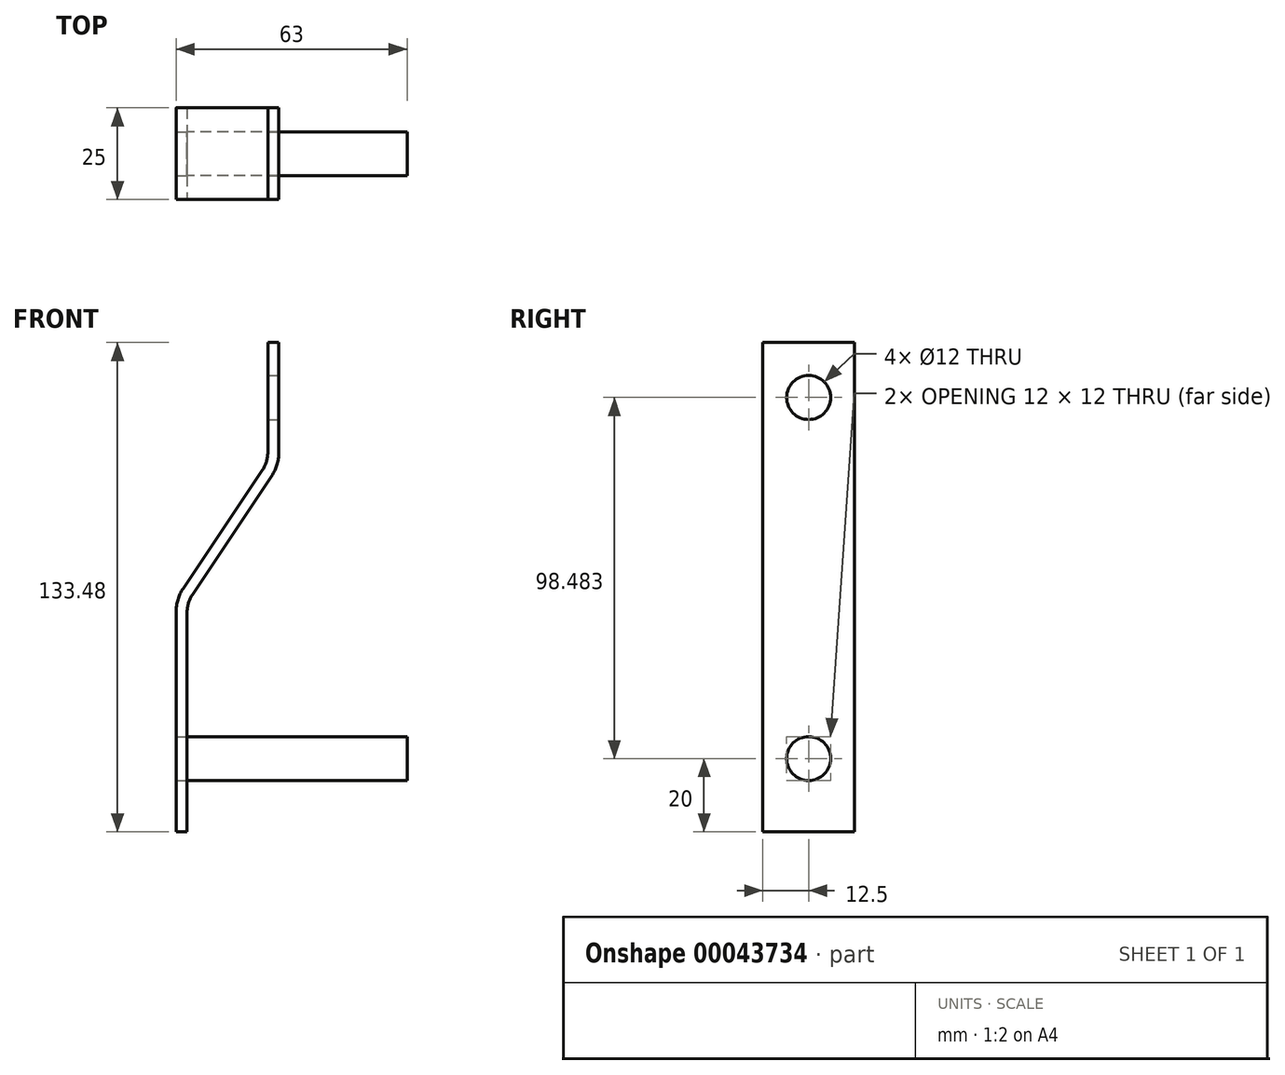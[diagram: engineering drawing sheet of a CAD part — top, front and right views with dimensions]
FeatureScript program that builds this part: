
annotation { "Feature Type Name" : "Feature", "Feature Type Description" : "" }
export const myFeature = defineFeature(function(context is Context, id is Id, definition is map)
    precondition{}
    {
        {
            var Q0;
            Q0=qCreatedBy(makeId("Top.planeOp"),FACE);
            var sketch = newSketch(context, id + "F0", { "sketchPlane" : qUnion([Q0])});
            skLineSegment(sketch, "E0.bottom", {"start": v(-1.5, 12.5) * mm, "end": v(1.5, 12.5) * mm});
            skLineSegment(sketch, "E0.top", {"start": v(-1.5, -12.5) * mm, "end": v(1.5, -12.5) * mm});
            skLineSegment(sketch, "E0.left", {"start": v(-1.5, 12.5) * mm, "end": v(-1.5, -12.5) * mm});
            skLineSegment(sketch, "E0.right", {"start": v(1.5, 12.5) * mm, "end": v(1.5, -12.5) * mm});
            skSolve(sketch);
        }
        {
            var Q0;
            Q0=qCreatedBy(makeId("Front.planeOp"),FACE);
            var sketch = newSketch(context, id + "F1", { "sketchPlane" : qUnion([Q0])});
            skLineSegment(sketch, "E1", {"start": v(0, 0) * mm, "end": v(0, 60) * mm});
            skLineSegment(sketch, "E2", {"start": v(1.69, 65.56) * mm, "end": v(23.31, 97.93) * mm});
            skLineSegment(sketch, "E3", {"start": v(25, 103.48) * mm, "end": v(25, 133.48) * mm});
            skPoint(sketch, "E4.visualSharp", {"position": v(25, 100.45) * mm});
            skArc(sketch, "E4.filletArc", {"start": v(23.31, 97.93) * mm, "mid": v(24.57, 100.58) * mm, "end": v(25, 103.48) * mm});
            skPoint(sketch, "E5.visualSharp", {"position": v(0, 63.03) * mm});
            skArc(sketch, "E5.filletArc", {"start": v(1.69, 65.56) * mm, "mid": v(0.43, 62.9) * mm, "end": v(0, 60) * mm});
            skSolve(sketch);
        }
        {
            var Q0;
            Q0=makeQuery(id+"F0.imprint","IMPRINT",FACE,{"disambiguationData":[TD([[makeQuery(id+"F0.imprint","IMPRINT",EDGE,{"derivedFrom":sQuery(id+"F0.wireOp",EDGE,"E0.bottom")}),-1.0]])]});
            var Q1;
            Q1=sQuery(id+"F1.wireOp",EDGE,"E1");
            var Q2;
            Q2=sQuery(id+"F1.wireOp",EDGE,"E5.filletArc");
            var Q3;
            Q3=sQuery(id+"F1.wireOp",EDGE,"E2");
            var Q4;
            Q4=sQuery(id+"F1.wireOp",EDGE,"E4.filletArc");
            var Q5;
            Q5=sQuery(id+"F1.wireOp",EDGE,"E3");
            sweep(context, id + "F2", {"profiles" : qUnion([Q0]), "path" : qUnion([Q1, Q2, Q3, Q4, Q5])});
        }
        {
            var Q0;
            Q0=makeQuery(id+"F2.opSweep","SWEPT_FACE",FACE,{"disambiguationData":[OSD([sQuery(id+"F0.wireOp",EDGE,"E0.right"),sQuery(id+"F1.wireOp",EDGE,"E1")])]});
            var sketch = newSketch(context, id + "F3", { "sketchPlane" : qUnion([Q0])});
            skCircle(sketch, "E6", {"center": v(0, 20) * mm, "radius": 6 * mm});
            skSolve(sketch);
        }
        {
            var Q0;
            Q0 = qSketchRegion(id + "F3", true);
            extrude(context, id + "F4", {"entities" : qUnion([Q0]), "operationType" : NewBodyOperationType.ADD, "depth" : 60 * mm});
        }
        {
            var Q0;
            Q0=makeQuery(id+"F2.opSweep","SWEPT_FACE",FACE,{"disambiguationData":[OSD([sQuery(id+"F0.wireOp",EDGE,"E0.right"),sQuery(id+"F1.wireOp",EDGE,"E3")])]});
            var sketch = newSketch(context, id + "F5", { "sketchPlane" : qUnion([Q0])});
            skCircle(sketch, "E7", {"center": v(0, 118.48) * mm, "radius": 6 * mm});
            skSolve(sketch);
        }
        {
            var Q0;
            Q0=makeQuery(id+"F5.imprint","IMPRINT",FACE,{"disambiguationData":[TD([[makeQuery(id+"F5.imprint","IMPRINT",EDGE,{"derivedFrom":sQuery(id+"F5.wireOp",EDGE,"E7")}),1.0]])]});
            extrude(context, id + "F6", {"entities" : qUnion([Q0]), "operationType" : NewBodyOperationType.REMOVE, "oppositeDirection" : true, "depth" : 25 * mm});
        }
        {
            var Q0;
            Q0=makeQuery(id+"F0.imprint","IMPRINT",FACE,{"disambiguationData":[TD([[makeQuery(id+"F0.imprint","IMPRINT",EDGE,{"derivedFrom":sQuery(id+"F0.wireOp",EDGE,"E0.bottom")}),-1.0]])]});
            var Q1;
            Q1=sQuery(id+"F1.wireOp",EDGE,"E1");
            var Q2;
            Q2=sQuery(id+"F1.wireOp",EDGE,"E5.filletArc");
            var Q3;
            Q3=sQuery(id+"F1.wireOp",EDGE,"E2");
            var Q4;
            Q4=sQuery(id+"F1.wireOp",EDGE,"E4.filletArc");
            var Q5;
            Q5=sQuery(id+"F1.wireOp",EDGE,"E3");
            sweep(context, id + "F7", {"profiles" : qUnion([Q0]), "path" : qUnion([Q1, Q2, Q3, Q4, Q5])});
        }
        {
            var Q0;
            Q0 = qSketchRegion(id + "F5", true);
            extrude(context, id + "F8", {"entities" : qUnion([Q0]), "operationType" : NewBodyOperationType.REMOVE, "oppositeDirection" : true, "depth" : 25 * mm});
        }
        {
            var Q0;
            Q0=makeQuery(id+"F3.imprint","IMPRINT",FACE,{"disambiguationData":[TD([[makeQuery(id+"F3.imprint","IMPRINT",EDGE,{"derivedFrom":sQuery(id+"F3.wireOp",EDGE,"E6")}),1.0]])]});
            extrude(context, id + "F9", {"entities" : qUnion([Q0]), "operationType" : NewBodyOperationType.REMOVE, "oppositeDirection" : true, "depth" : 25 * mm});
        }
    });
